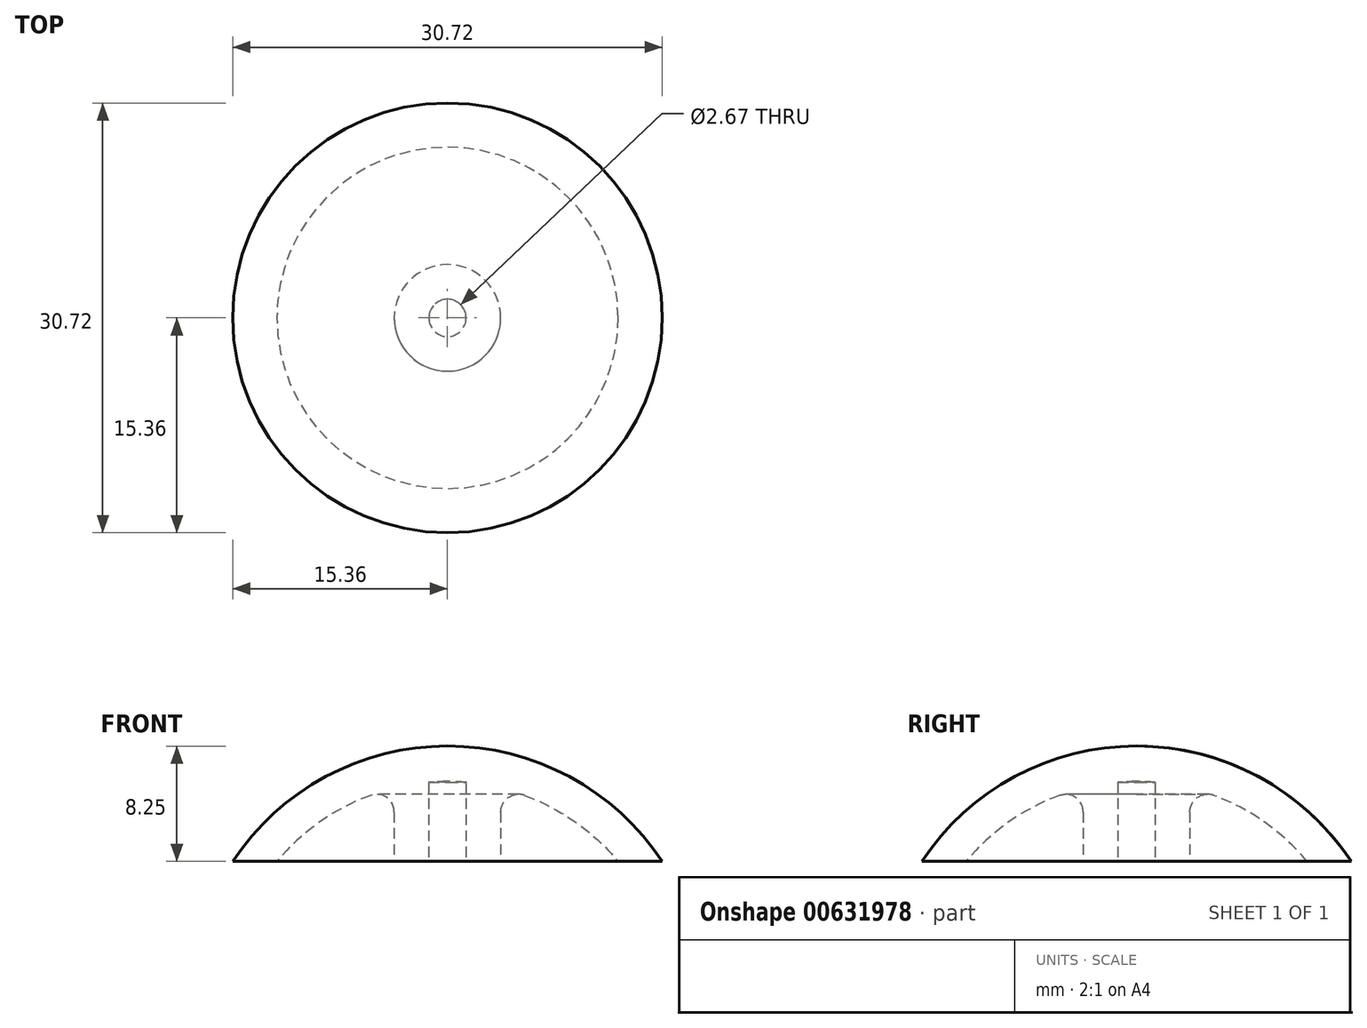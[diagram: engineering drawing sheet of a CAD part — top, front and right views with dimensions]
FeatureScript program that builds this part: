
annotation { "Feature Type Name" : "Feature", "Feature Type Description" : "" }
export const myFeature = defineFeature(function(context is Context, id is Id, definition is map)
    precondition{}
    {
        {
            var Q0;
            Q0=qCreatedBy(makeId("Top.planeOp"),FACE);
            var sketch = newSketch(context, id + "F0", { "sketchPlane" : qUnion([Q0])});
            skCircle(sketch, "E0", {"center": v(0, 0) * mm, "radius": 18.41 * mm});
            skSolve(sketch);
        }
        {
            var Q0;
            Q0=qCreatedBy(makeId("Right.planeOp"),FACE);
            var sketch = newSketch(context, id + "F1", { "sketchPlane" : qUnion([Q0])});
            skLineSegment(sketch, "E1", {"start": v(0, 0) * mm, "end": v(0, 18.41) * mm});
            skLineSegment(sketch, "E2", {"start": v(0, 0) * mm, "end": v(18.41, 0) * mm});
            skArc(sketch, "E3", {"start": v(18.41, 0) * mm, "mid": v(13.02, 13.02) * mm, "end": v(0, 18.41) * mm});
            skSolve(sketch);
        }
        {
            var Q0;
            Q0 = qSketchRegion(id + "F1", true);
            var Q1;
            Q1=sQuery(id+"F1.wireOp",EDGE,"E1");
            revolve(context, id + "F2", {"entities" : qUnion([Q0]), "axis" : qUnion([Q1]), "revolveType" : RevolveType.FULL});
        }
        {
            var Q0;
            Q0=makeQuery(id+"F2.opRevolve","SWEPT_FACE",FACE,{"disambiguationData":[OSD([sQuery(id+"F1.wireOp",EDGE,"E2")])]});
            shell(context, id + "F3", {"entities" : qUnion([Q0]), "thickness" : 2.54 * mm});
        }
        {
            var Q0;
            Q0=makeQuery(id+"F0.imprint","IMPRINT",FACE,{"disambiguationData":[TD([[makeQuery(id+"F0.imprint","IMPRINT",EDGE,{"derivedFrom":sQuery(id+"F0.wireOp",EDGE,"E0")}),1.0]])]});
            var sketch = newSketch(context, id + "F4", { "sketchPlane" : qUnion([Q0])});
            skCircle(sketch, "E4", {"center": v(0, 0) * mm, "radius": 3.81 * mm});
            skCircle(sketch, "E5", {"center": v(0, 0) * mm, "radius": 1.33 * mm});
            skSolve(sketch);
        }
        {
            var Q0;
            Q0 = qSketchRegion(id + "F4", true);
            var Q1;
            Q1=makeQuery(id+"F3.opShell","OFFSET_FACE",FACE,{"disambiguationData":[OSD([sQuery(id+"F1.wireOp",EDGE,"E3")])]});
            extrude(context, id + "F5", {"entities" : qUnion([Q0]), "operationType" : NewBodyOperationType.ADD, "endBound" : BoundingType.UP_TO_SURFACE, "depth" : 25.4 * mm, "endBoundEntityFace" : qUnion([Q1]), "offsetDistance" : 25.4 * mm});
        }
        {
            var Q0;
            Q0=makeQuery(id+"F5.opExtrude","CAP_EDGE",EDGE,{"disambiguationData":[OSD([sQuery(id+"F4.wireOp",EDGE,"E4")])],"isStart":false});
            fillet(context, id + "F6", {"entities" : qUnion([Q0]), "radius" : 1.27 * mm, "tangentPropagation" : true, "allowEdgeOverflow" : false});
        }
        {
            var Q0;
            Q0=makeQuery(id+"F0.imprint","IMPRINT",FACE,{"disambiguationData":[TD([[makeQuery(id+"F0.imprint","IMPRINT",EDGE,{"derivedFrom":sQuery(id+"F0.wireOp",EDGE,"E0")}),1.0]])]});
            var sketch = newSketch(context, id + "F7", { "sketchPlane" : qUnion([Q0])});
            skCircle(sketch, "E6", {"center": v(0, 0) * mm, "radius": 18.41 * mm});
            skSolve(sketch);
        }
        {
            var Q0;
            Q0 = qSketchRegion(id + "F7", true);
            extrude(context, id + "F8", {"entities" : qUnion([Q0]), "operationType" : NewBodyOperationType.REMOVE, "depth" : 10.16 * mm, "offsetDistance" : 25.4 * mm});
        }
    });
